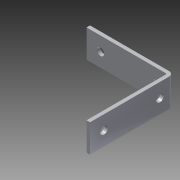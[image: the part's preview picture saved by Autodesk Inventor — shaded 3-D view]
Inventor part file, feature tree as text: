
AUTODESK INVENTOR PART (.ipt)
format: ipt  version: 2014 SP1 (Build 180222100, 222)  size: 165,888 bytes
history: native  units: in
note: dims shown in document units (in); Inventor stores cm internally (conversion verified against a paired STEP export)
features: other x4, sheet_metal_op x3, sketch x3
ambient origin geometry x8: Origin, YZ Plane, XZ Plane, XY Plane, X Axis, Y Axis, Z Axis, Center Point
bodies: Solid1 (feature_tree)
feature tree (10):
  sheet_metal_op  "Face1"
  sheet_metal_op  "Flange1"
  sketch  "Sketch1"  dims[d0=1.0in]
  other  "Plate1"
  sketch  "Sketch2"  dims[d1=3.0in]
  other  "Plate2"
  sheet_metal_op  "Bend1"
  sketch  "Sketch3"  dims[d2=0.266in d3=0.266in d4=0.5in d5=0.5in d6=0.5in d7=0.5in d8=0.125in d9=0.125in d10=0.0625in d11=0.25in d12=0.125in d13=3.0in d14=90.0deg d15=0.05in d16=0.5in d17=0.125in d18=0.125in d19=0.266in d20=0.266in d22=0.5in d23=0.5in d24=0.5in d25=0.125in d26=0.0in d27=2.0in]
  other  "Cut1"
  other  "Definition1"
